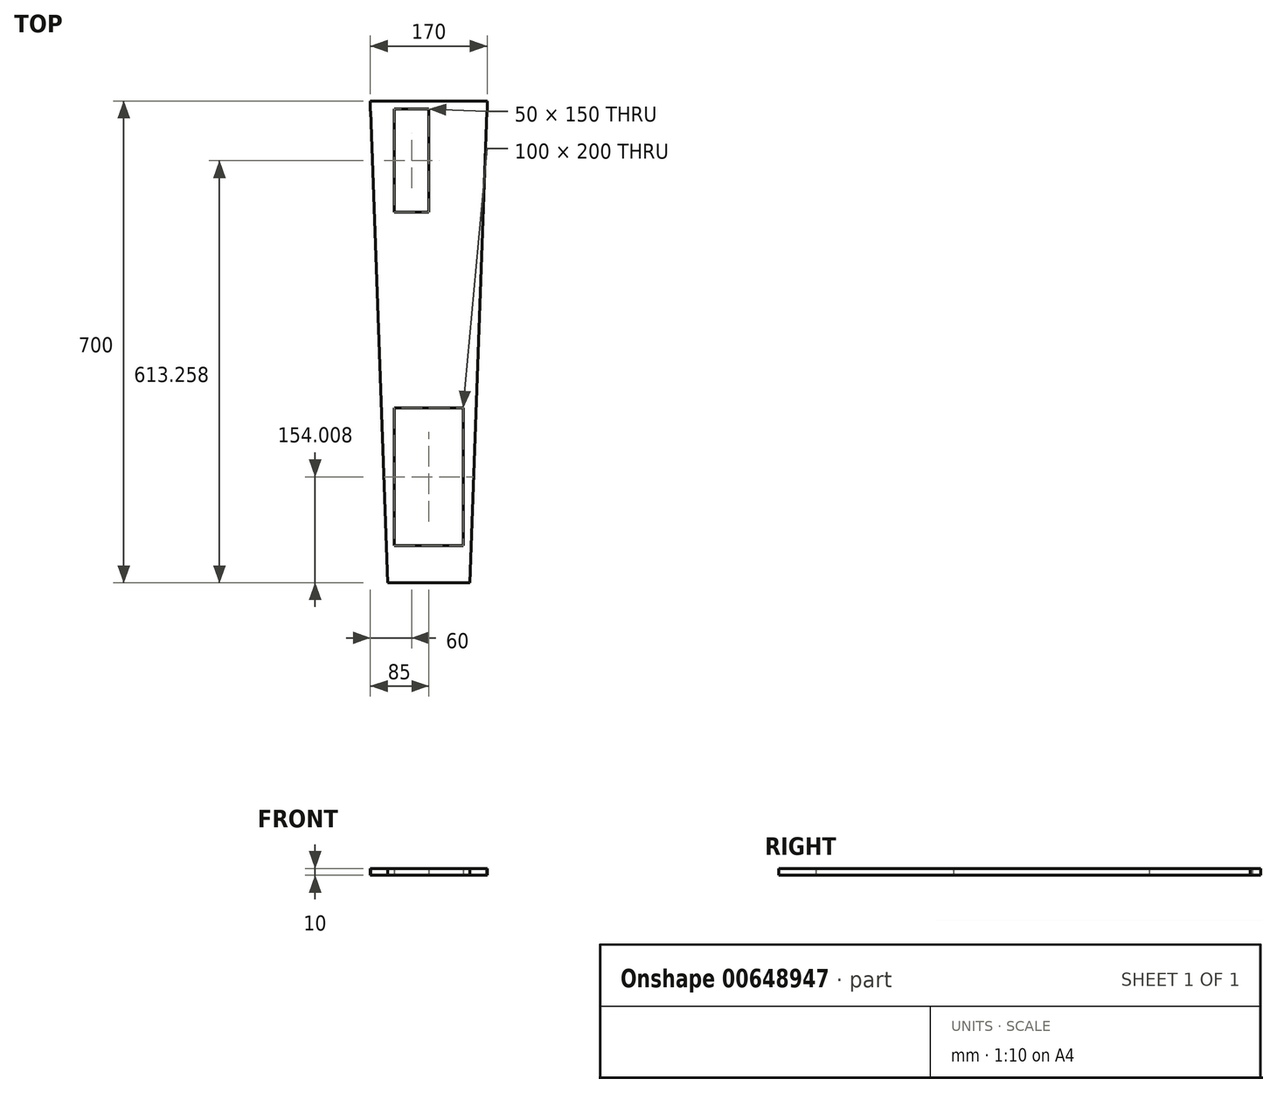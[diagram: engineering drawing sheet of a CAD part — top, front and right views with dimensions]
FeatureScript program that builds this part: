
annotation { "Feature Type Name" : "Feature", "Feature Type Description" : "" }
export const myFeature = defineFeature(function(context is Context, id is Id, definition is map)
    precondition{}
    {
        {
            var Q0;
            Q0=qCreatedBy(makeId("Top.planeOp"),FACE);
            var sketch = newSketch(context, id + "F0", { "sketchPlane" : qUnion([Q0])});
            skLineSegment(sketch, "E0.bottom", {"start": v(85, -7.5) * mm, "end": v(-85, -7.5) * mm});
            skLineSegment(sketch, "E0.top", {"start": v(85, 7.5) * mm, "end": v(-85, 7.5) * mm});
            skLineSegment(sketch, "E0.left", {"start": v(85, -7.5) * mm, "end": v(85, 7.5) * mm});
            skLineSegment(sketch, "E0.right", {"start": v(-85, -7.5) * mm, "end": v(-85, 7.5) * mm});
            skPoint(sketch, "E0.middle", {"position": v(0, 0) * mm});
            skLineSegment(sketch, "E1.bottom", {"start": v(60, -670.57) * mm, "end": v(-60, -670.57) * mm});
            skLineSegment(sketch, "E1.top", {"start": v(60, -692.5) * mm, "end": v(-60, -692.5) * mm});
            skLineSegment(sketch, "E1.left", {"start": v(60, -670.57) * mm, "end": v(60, -692.5) * mm});
            skLineSegment(sketch, "E1.right", {"start": v(-60, -670.57) * mm, "end": v(-60, -692.5) * mm});
            skPoint(sketch, "E1.middle", {"position": v(0, -681.54) * mm});
            skLineSegment(sketch, "E2", {"start": v(85, 7.5) * mm, "end": v(60, -692.5) * mm});
            skLineSegment(sketch, "E3", {"start": v(-85, 7.5) * mm, "end": v(-60, -692.5) * mm});
            skLineSegment(sketch, "E4.bottom", {"start": v(50, -438.5) * mm, "end": v(-50, -438.5) * mm});
            skLineSegment(sketch, "E4.top", {"start": v(50, -638.5) * mm, "end": v(-50, -638.5) * mm});
            skLineSegment(sketch, "E4.left", {"start": v(50, -438.5) * mm, "end": v(50, -638.5) * mm});
            skLineSegment(sketch, "E4.right", {"start": v(-50, -438.5) * mm, "end": v(-50, -638.5) * mm});
            skPoint(sketch, "E4.middle", {"position": v(0, -538.5) * mm});
            skPoint(sketch, "E5.firstSnap0", {"position": v(0, -7.5) * mm});
            skLineSegment(sketch, "E5.bottom", {"start": v(0, -4.24) * mm, "end": v(-50, -4.24) * mm});
            skLineSegment(sketch, "E5.top", {"start": v(0, -154.24) * mm, "end": v(-50, -154.24) * mm});
            skLineSegment(sketch, "E5.left", {"start": v(0, -4.24) * mm, "end": v(0, -154.24) * mm});
            skLineSegment(sketch, "E5.right", {"start": v(-50, -4.24) * mm, "end": v(-50, -154.24) * mm});
            skSolve(sketch);
        }
        {
            var Q0;
            Q0=qSketchRegion(id+"F0",true);
            extrude(context, id + "F1", {"entities" : qUnion([Q0]), "depth" : 10 * mm, "offsetDistance" : 25 * mm});
        }
    });
